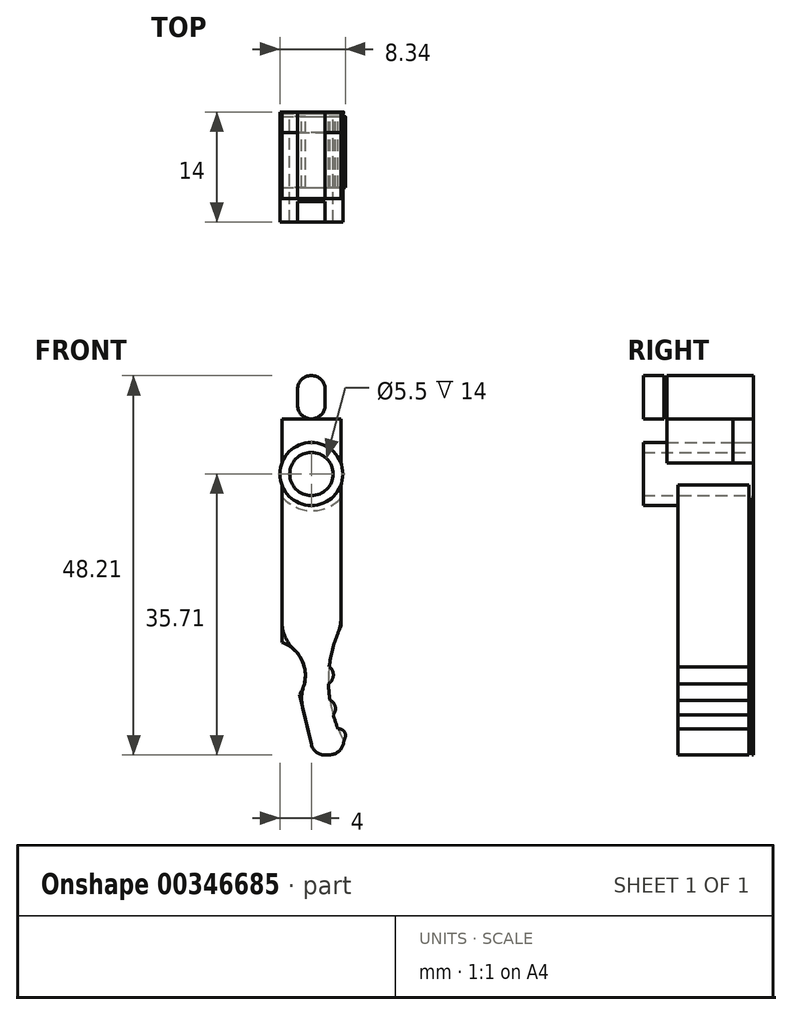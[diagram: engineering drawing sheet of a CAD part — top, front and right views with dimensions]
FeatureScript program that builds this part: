
annotation { "Feature Type Name" : "Feature", "Feature Type Description" : "" }
export const myFeature = defineFeature(function(context is Context, id is Id, definition is map)
    precondition{}
    {
        {
            var Q0;
            Q0=qCreatedBy(makeId("Front.planeOp"),FACE);
            var sketch = newSketch(context, id + "F0", { "sketchPlane" : qUnion([Q0])});
            skCircle(sketch, "E0", {"center": v(0, 0) * mm, "radius": 2.75 * mm});
            skCircle(sketch, "E1", {"center": v(0, 0) * mm, "radius": 4 * mm});
            skLineSegment(sketch, "E2", {"start": v(0, 0) * mm, "end": v(0, 14) * mm});
            skLineSegment(sketch, "E3", {"start": v(0, 7) * mm, "end": v(-3.75, 7) * mm});
            skPoint(sketch, "E3.endSnap0", {"position": v(0, 7) * mm});
            skLineSegment(sketch, "E4", {"start": v(0, 7) * mm, "end": v(3.75, 7) * mm});
            skLineSegment(sketch, "E5", {"start": v(-0.25, 14) * mm, "end": v(0.25, 14) * mm});
            skLineSegment(sketch, "E6", {"start": v(3.75, 1.4) * mm, "end": v(3.75, 10.5) * mm});
            skLineSegment(sketch, "E7", {"start": v(-3.75, 1.4) * mm, "end": v(-3.75, 10.5) * mm});
            skPoint(sketch, "E8.newPointB", {"position": v(-3.66, 14) * mm});
            skArc(sketch, "E8.filletArc", {"start": v(-0.25, 14) * mm, "mid": v(-2.72, 12.97) * mm, "end": v(-3.75, 10.5) * mm});
            skArc(sketch, "E9.filletArc", {"start": v(3.75, 10.5) * mm, "mid": v(2.72, 12.97) * mm, "end": v(0.25, 14) * mm});
            skLineSegment(sketch, "E10", {"start": v(0, 0) * mm, "end": v(0, 12.5) * mm});
            skLineSegment(sketch, "E11", {"start": v(0, 12.5) * mm, "end": v(0, 7) * mm});
            skLineSegment(sketch, "E12", {"start": v(0, 7) * mm, "end": v(0, 7) * mm});
            skLineSegment(sketch, "E13", {"start": v(0, 12.5) * mm, "end": v(0, 12.5) * mm});
            skLineSegment(sketch, "E14", {"start": v(-1.75, 8.75) * mm, "end": v(-1.75, 10.75) * mm});
            skLineSegment(sketch, "E15", {"start": v(1.75, 10.75) * mm, "end": v(1.75, 8.75) * mm});
            skPoint(sketch, "E16.visualSharp", {"position": v(-1.75, 12.5) * mm});
            skArc(sketch, "E16.filletArc", {"start": v(0, 12.5) * mm, "mid": v(-1.24, 11.99) * mm, "end": v(-1.75, 10.75) * mm});
            skPoint(sketch, "E17.visualSharp", {"position": v(1.75, 12.5) * mm});
            skArc(sketch, "E17.filletArc", {"start": v(1.75, 10.75) * mm, "mid": v(1.24, 11.99) * mm, "end": v(0, 12.5) * mm});
            skPoint(sketch, "E18.visualSharp", {"position": v(1.75, 7) * mm});
            skArc(sketch, "E18.filletArc", {"start": v(0, 7) * mm, "mid": v(1.24, 7.51) * mm, "end": v(1.75, 8.75) * mm});
            skPoint(sketch, "E19.visualSharp", {"position": v(-1.75, 7) * mm});
            skArc(sketch, "E19.filletArc", {"start": v(-1.75, 8.75) * mm, "mid": v(-1.24, 7.51) * mm, "end": v(0, 7) * mm});
            skLineSegment(sketch, "E20", {"start": v(-3.75, -1.4) * mm, "end": v(-3.75, -21.4) * mm});
            skLineSegment(sketch, "E21", {"start": v(3.75, -1.4) * mm, "end": v(3.75, -19.4) * mm});
            skLineSegment(sketch, "E22", {"start": v(-3.75, -21.4) * mm, "end": v(-1.5, -28.02) * mm});
            skArc(sketch, "E23", {"start": v(-1.5, -28.02) * mm, "mid": v(-1, -24.15) * mm, "end": v(-3.75, -21.4) * mm});
            skPoint(sketch, "E24", {"position": v(-1, -24.15) * mm});
            skLineSegment(sketch, "E25", {"start": v(-1.5, -28.02) * mm, "end": v(0, -34.36) * mm});
            skLineSegment(sketch, "E26", {"start": v(1.82, -35.7) * mm, "end": v(2.46, -35.66) * mm});
            skPoint(sketch, "E27.visualSharp", {"position": v(0.34, -35.8) * mm});
            skArc(sketch, "E27.filletArc", {"start": v(0, -34.36) * mm, "mid": v(0.66, -35.37) * mm, "end": v(1.82, -35.7) * mm});
            skPoint(sketch, "E28.visualSharp", {"position": v(4.2, -35.54) * mm});
            skArc(sketch, "E28.filletArc", {"start": v(2.46, -35.66) * mm, "mid": v(3.66, -35.07) * mm, "end": v(4.1, -33.81) * mm});
            skArc(sketch, "E29", {"start": v(3.75, -19.4) * mm, "mid": v(2.17, -26.64) * mm, "end": v(4.1, -33.81) * mm});
            skArc(sketch, "E30", {"start": v(4.1, -33.81) * mm, "mid": v(4.26, -32.85) * mm, "end": v(3.4, -32.38) * mm});
            skArc(sketch, "E31", {"start": v(2.77, -30.57) * mm, "mid": v(3.04, -29.57) * mm, "end": v(2.37, -28.77) * mm});
            skArc(sketch, "E32", {"start": v(2.17, -26.64) * mm, "mid": v(2.8, -25.59) * mm, "end": v(2.27, -24.48) * mm});
            skArc(sketch, "E33", {"start": v(-3.75, -2.81) * mm, "mid": v(-0.05, -4.67) * mm, "end": v(3.75, -3.04) * mm});
            skArc(sketch, "E34", {"start": v(3.75, 2.74) * mm, "mid": v(-0.02, 4.4) * mm, "end": v(-3.75, 2.66) * mm});
            skSolve(sketch);
        }
        {
            var Q0;
            {var subQ0=sQuery(id+"F0.wireOp",EDGE,"E32");Q0=makeQuery(id+"F0.imprint","IMPRINT",FACE,{"disambiguationData":[TD([[makeQuery(id+"F0.imprint","IMPRINT",EDGE,{"derivedFrom":subQ0}),1.0]])]});}
            var Q1;
            {var subQ0=sQuery(id+"F0.wireOp",EDGE,"E31");Q1=makeQuery(id+"F0.imprint","IMPRINT",FACE,{"disambiguationData":[TD([[makeQuery(id+"F0.imprint","IMPRINT",EDGE,{"derivedFrom":subQ0}),1.0]])]});}
            var Q2;
            {var subQ0=sQuery(id+"F0.wireOp",EDGE,"E30");Q2=makeQuery(id+"F0.imprint","IMPRINT",FACE,{"disambiguationData":[TD([[makeQuery(id+"F0.imprint","IMPRINT",EDGE,{"derivedFrom":subQ0}),1.0]])]});}
            var Q3;
            {var subQ6=sQuery(id+"F0.wireOp",EDGE,"E20");Q3=makeQuery(id+"F0.imprint","IMPRINT",FACE,{"disambiguationData":[TD([[makeQuery(id+"F0.imprint","IMPRINT",EDGE,{"derivedFrom":subQ6}),1.0]])]});}
            var Q4;
            {var subQ9=sQuery(id+"F0.wireOp",EDGE,"E23");Q4=makeQuery(id+"F0.imprint","IMPRINT",FACE,{"disambiguationData":[TD([[makeQuery(id+"F0.imprint","IMPRINT",EDGE,{"derivedFrom":subQ9}),-1.0]])]});}
            extrude(context, id + "F1", {"entities" : qUnion([Q0, Q1, Q2, Q3, Q4]), "depth" : 9 * mm});
        }
        {
            var Q0;
            Q0=makeQuery(id+"F1.opExtrude","SWEPT_BODY",BODY,{"disambiguationData":[OSD([sQuery(id+"F0.wireOp",EDGE,"E1"),sQuery(id+"F0.wireOp",EDGE,"E20"),sQuery(id+"F0.wireOp",EDGE,"E21"),sQuery(id+"F0.wireOp",EDGE,"E23"),sQuery(id+"F0.wireOp",EDGE,"E25"),sQuery(id+"F0.wireOp",EDGE,"E26"),sQuery(id+"F0.wireOp",EDGE,"E27.filletArc"),sQuery(id+"F0.wireOp",EDGE,"E28.filletArc"),sQuery(id+"F0.wireOp",EDGE,"E29"),sQuery(id+"F0.wireOp",EDGE,"E30"),sQuery(id+"F0.wireOp",EDGE,"E31"),sQuery(id+"F0.wireOp",EDGE,"E32")])]});
            transform(context, id + "F2", {"entities" : qUnion([Q0]), "transformType" : TransformType.TRANSLATION_3D, "dx" : 0 * mm, "dy" : -0.6 * mm, "dz" : 0 * mm, "makeCopy" : false});
        }
        {
            var Q0;
            Q0=makeQuery(id+"F0.imprint","IMPRINT",FACE,{"disambiguationData":[TD([[makeQuery(id+"F0.imprint","IMPRINT",EDGE,{"derivedFrom":sQuery(id+"F0.wireOp",EDGE,"E0")}),-1.0]])]});
            extrude(context, id + "F3", {"entities" : qUnion([Q0]), "operationType" : NewBodyOperationType.ADD, "depth" : 14 * mm});
        }
        {
            var Q0;
            {var subQ4=sQuery(id+"F0.wireOp",EDGE,"E2");Q0=makeQuery(id+"F0.imprint","IMPRINT",FACE,{"disambiguationData":[TD([[makeQuery(id+"F0.imprint","IMPRINT",EDGE,{"derivedFrom":subQ4}),1.0]])]});}
            var Q1;
            {var subQ5=sQuery(id+"F0.wireOp",EDGE,"E3");Q1=makeQuery(id+"F0.imprint","IMPRINT",FACE,{"disambiguationData":[TD([[makeQuery(id+"F0.imprint","IMPRINT",EDGE,{"derivedFrom":subQ5}),1.0]])]});}
            var Q2;
            {var subQ5=sQuery(id+"F0.wireOp",EDGE,"E4");Q2=makeQuery(id+"F0.imprint","IMPRINT",FACE,{"disambiguationData":[TD([[makeQuery(id+"F0.imprint","IMPRINT",EDGE,{"derivedFrom":subQ5}),-1.0]])]});}
            var Q3;
            {var subQ4=sQuery(id+"F0.wireOp",EDGE,"E2");Q3=makeQuery(id+"F0.imprint","IMPRINT",FACE,{"disambiguationData":[TD([[makeQuery(id+"F0.imprint","IMPRINT",EDGE,{"derivedFrom":subQ4}),-1.0]])]});}
            var Q4;
            {var subQ0=sQuery(id+"F0.wireOp",EDGE,"E7");var subQ1=sQuery(id+"F0.wireOp",EDGE,"E1");var subQ2=makeQuery(id+"F0.imprint","INTERSECT",VERTEX,{"derivedFrom":[subQ1,subQ0]});Q4=makeQuery(id+"F0.imprint","IMPRINT",FACE,{"disambiguationData":[TD([[makeQuery(id+"F0.imprint","IMPRINT",EDGE,{"disambiguationData":[TD([[subQ2,1.0]])],"derivedFrom":subQ1}),-1.0]])]});}
            var Q5;
            {var subQ0=sQuery(id+"F0.wireOp",EDGE,"E6");var subQ1=sQuery(id+"F0.wireOp",EDGE,"E1");var subQ2=makeQuery(id+"F0.imprint","INTERSECT",VERTEX,{"derivedFrom":[subQ1,subQ0]});Q5=makeQuery(id+"F0.imprint","IMPRINT",FACE,{"disambiguationData":[TD([[makeQuery(id+"F0.imprint","IMPRINT",EDGE,{"disambiguationData":[TD([[subQ2,-1.0]])],"derivedFrom":subQ1}),-1.0]])]});}
            extrude(context, id + "F4", {"entities" : qUnion([Q0, Q1, Q2, Q3, Q4, Q5]), "depth" : 2.6 * mm});
        }
        {
            var Q0;
            Q0=makeQuery(id+"F4.opExtrude","SWEPT_BODY",BODY,{"disambiguationData":[OSD([sQuery(id+"F0.wireOp",EDGE,"E1"),sQuery(id+"F0.wireOp",EDGE,"E5"),sQuery(id+"F0.wireOp",EDGE,"E6"),sQuery(id+"F0.wireOp",EDGE,"E7"),sQuery(id+"F0.wireOp",EDGE,"E8.filletArc"),sQuery(id+"F0.wireOp",EDGE,"E9.filletArc"),sQuery(id+"F0.wireOp",EDGE,"E14"),sQuery(id+"F0.wireOp",EDGE,"E15"),sQuery(id+"F0.wireOp",EDGE,"E16.filletArc"),sQuery(id+"F0.wireOp",EDGE,"E17.filletArc"),sQuery(id+"F0.wireOp",EDGE,"E18.filletArc"),sQuery(id+"F0.wireOp",EDGE,"E19.filletArc")])]});
            transform(context, id + "F5", {"entities" : qUnion([Q0]), "transformType" : TransformType.TRANSLATION_3D, "dx" : 0 * mm, "dy" : -11.4 * mm, "dz" : 0 * mm, "makeCopy" : false});
        }
        {
            var Q0;
            Q0=makeQuery(id+"F1.opExtrude","SWEPT_EDGE",EDGE,{"disambiguationData":[OSD([sQuery(id+"F0.wireOp",EDGE,"E20"),sQuery(id+"F0.wireOp",EDGE,"E22"),sQuery(id+"F0.wireOp",EDGE,"E23")])]});
            var Q1;
            Q1=makeQuery(id+"F1.opExtrude","SWEPT_EDGE",EDGE,{"disambiguationData":[OSD([sQuery(id+"F0.wireOp",EDGE,"E22"),sQuery(id+"F0.wireOp",EDGE,"E23"),sQuery(id+"F0.wireOp",EDGE,"E25")])]});
            var Q2;
            Q2=makeQuery(id+"F1.opExtrude","SWEPT_EDGE",EDGE,{"disambiguationData":[OSD([sQuery(id+"F0.wireOp",EDGE,"E28.filletArc"),sQuery(id+"F0.wireOp",EDGE,"E29"),sQuery(id+"F0.wireOp",EDGE,"E30")])]});
            var Q3;
            Q3=makeQuery(id+"F1.opExtrude","SWEPT_EDGE",EDGE,{"disambiguationData":[OSD([sQuery(id+"F0.wireOp",EDGE,"E21"),sQuery(id+"F0.wireOp",EDGE,"E29")])]});
            fillet(context, id + "F6", {"entities" : qUnion([Q0, Q1, Q2, Q3]), "radius" : 5 * mm, "tangentPropagation" : true, "allowEdgeOverflow" : false});
        }
        {
            var Q0;
            {var subQ9=sQuery(id+"F0.wireOp",EDGE,"E23");Q0=makeQuery(id+"F0.imprint","IMPRINT",FACE,{"disambiguationData":[TD([[makeQuery(id+"F0.imprint","IMPRINT",EDGE,{"derivedFrom":subQ9}),-1.0]])]});}
            extrude(context, id + "F7", {"entities" : qUnion([Q0]), "depth" : .2 * mm});
        }
        {
            var Q0;
            {var subQ0=sQuery(id+"F0.wireOp",EDGE,"E4");Q0=makeQuery(id+"F0.imprint","IMPRINT",FACE,{"disambiguationData":[TD([[makeQuery(id+"F0.imprint","IMPRINT",EDGE,{"derivedFrom":subQ0}),-1.0]])]});}
            var Q1;
            {var subQ0=sQuery(id+"F0.wireOp",EDGE,"E3");Q1=makeQuery(id+"F0.imprint","IMPRINT",FACE,{"disambiguationData":[TD([[makeQuery(id+"F0.imprint","IMPRINT",EDGE,{"derivedFrom":subQ0}),1.0]])]});}
            var Q2;
            {var subQ1=sQuery(id+"F0.wireOp",EDGE,"E2");Q2=makeQuery(id+"F0.imprint","IMPRINT",FACE,{"disambiguationData":[TD([[makeQuery(id+"F0.imprint","IMPRINT",EDGE,{"derivedFrom":subQ1}),1.0]])]});}
            var Q3;
            {var subQ1=sQuery(id+"F0.wireOp",EDGE,"E2");Q3=makeQuery(id+"F0.imprint","IMPRINT",FACE,{"disambiguationData":[TD([[makeQuery(id+"F0.imprint","IMPRINT",EDGE,{"derivedFrom":subQ1}),-1.0]])]});}
            extrude(context, id + "F8", {"entities" : qUnion([Q0, Q1, Q2, Q3]), "depth" : 11 * mm});
        }
    });
